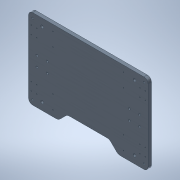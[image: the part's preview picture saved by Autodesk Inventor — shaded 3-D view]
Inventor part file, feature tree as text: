
AUTODESK INVENTOR PART (.ipt)
format: ipt  version: 2020.3 (Build 243373000, 373)  size: 262,656 bytes
history: native  units: in
note: dims shown in document units (in); Inventor stores cm internally (conversion verified against a paired STEP export)
features: hole x5, sketch x3, extrude x2, fillet x2, chamfer x1, projected_geometry x1
ambient origin geometry x8: Origin, YZ Plane, XZ Plane, XY Plane, X Axis, Y Axis, Z Axis, Center Point
bodies: Solid1 (feature_tree)
feature tree (14):
  extrude  "Extrusion1"  Depth=14.75in
  hole  "Hole1"  [1 undecoded]
  hole  "Hole2"  [1 undecoded]
  hole  "Hole3"  [1 undecoded]
  extrude  "Extrusion2"  Depth=0.75in
  chamfer  "Chamfer1"  [1 undecoded]
  fillet  "Fillet2"  [1 undecoded]
  fillet  "Fillet1"  [1 undecoded]
  hole  "Hole4"  [1 undecoded]
  hole  "Hole5"  [1 undecoded]
  sketch  "Sketch2"  dims[d0=22.0in d1=14.75in]
  sketch  "Sketch3"  dims[d2=17.0in d3=12.0in]
  projected_geometry  "Projected Loop1"
  sketch  "Sketch5"  dims[d4=20.0in d5=8.0in d7=0.625in d8=0.0in d9=0.551in d10=0.625in d11=0.375in d12=0.25in d13=0.5635in d14=0.903in d15=0.8108in d16=0.75in d17=0.0in d18=0.0in d21=0.228in d22=0.394in d23=0.394in d24=0.25in d25=0.5635in d26=0.559in d27=0.8108in d28=0.0in d29=12.5in d30=13.0in d31=0.156in d32=0.38in d33=0.375in d34=0.25in d35=0.5635in d36=0.536in d37=0.8108in d38=8.5in d39=8.5in d40=1.902in d41=1.902in d42=1.902in d43=1.902in d44=1.625in d45=11.0in d46=1.0in d47=0.0in d48=1.625in d49=0.125in d50=45.0deg d51=1.0in d52=20.5in d53=13.0in d54=0.332in d55=0.75in d56=0.119in d57=0.25in d58=0.5635in d59=1.0in d60=0.8108in d61=1.5748in d62=0.9449in d63=2.5in d64=2.5in d65=2.5in d66=2.5in d67=3.0in d68=3.0in d69=3.0in d70=3.0in d71=7.813in d72=11.5in d73=11.5in d74=0.0667in d75=0.172in d76=0.375in d77=0.25in d78=0.5635in d79=0.3in d80=0.8108in d81=1.5in d82=1.5in d83=1.5in d84=1.5in d85=1.0in d86=1.0in]
note: 8 required parameter values undecoded (feature->parameter linkage not recoverable at this tier; creation-order binding heuristic only, values carry confidence <= 0.55)
